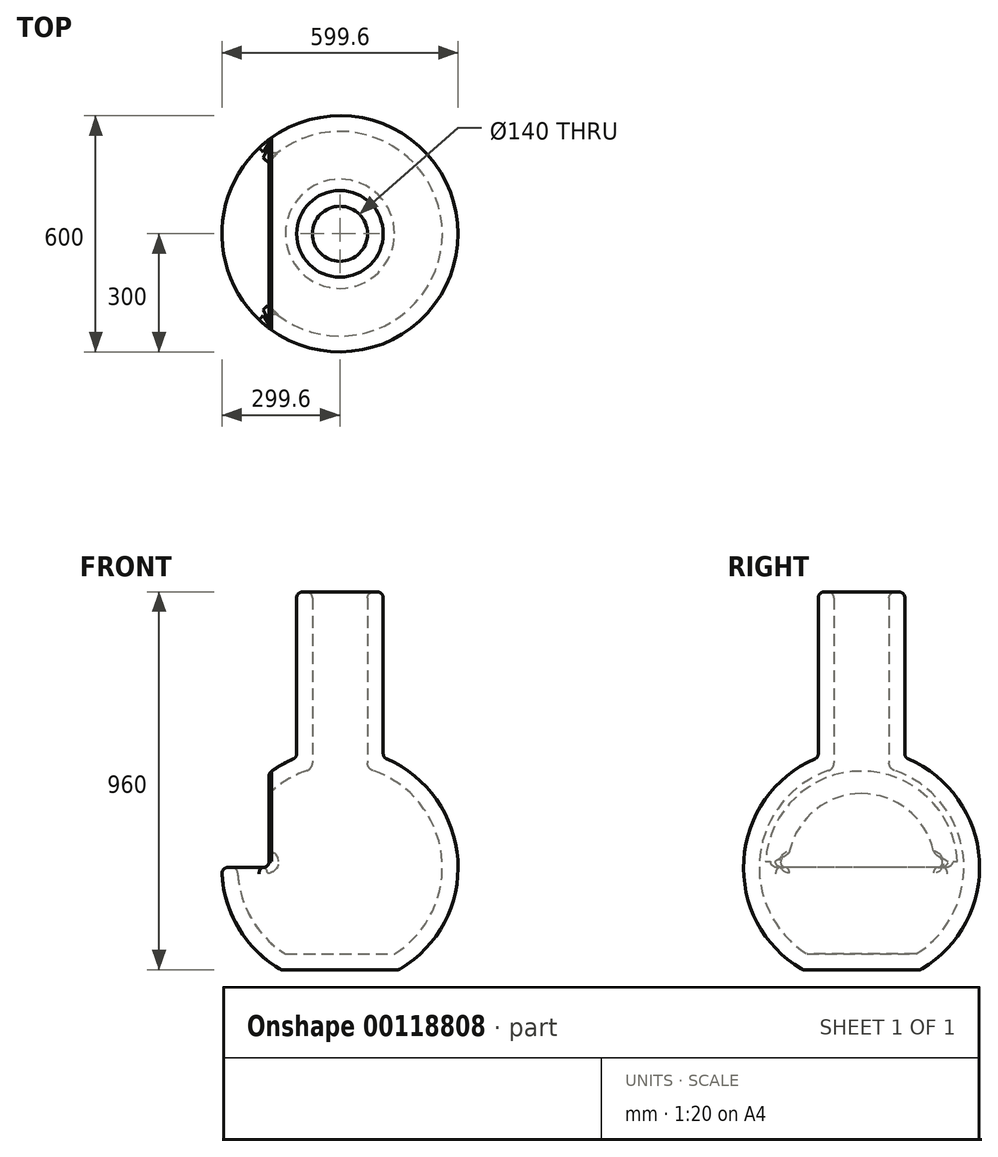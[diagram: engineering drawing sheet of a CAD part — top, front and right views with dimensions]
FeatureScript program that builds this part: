
annotation { "Feature Type Name" : "Feature", "Feature Type Description" : "" }
export const myFeature = defineFeature(function(context is Context, id is Id, definition is map)
    precondition{}
    {
        {
            var Q0;
            Q0=qCreatedBy(makeId("Front.planeOp"),FACE);
            var sketch = newSketch(context, id + "F0", { "sketchPlane" : qUnion([Q0])});
            skArc(sketch, "E0", {"start": v(0, 300) * mm, "mid": v(-254.47, 158.89) * mm, "end": v(-269.55, -131.7) * mm});
            skLineSegment(sketch, "E1", {"start": v(0, -260) * mm, "end": v(0, 700) * mm});
            skLineSegment(sketch, "E2", {"start": v(0, 700) * mm, "end": v(-110, 700) * mm});
            skLineSegment(sketch, "E3", {"start": v(-110, 700) * mm, "end": v(-110, 279.1) * mm});
            skLineSegment(sketch, "E4", {"start": v(0, 0) * mm, "end": v(-300, 0) * mm});
            skLineSegment(sketch, "E5", {"start": v(0, -260) * mm, "end": v(-149.67, -260) * mm});
            skLineSegment(sketch, "E6", {"start": v(0, -131.7) * mm, "end": v(-269.55, -131.7) * mm});
            skLineSegment(sketch, "E7", {"start": v(-180, 240) * mm, "end": v(-180, 0) * mm});
            skLineSegment(sketch, "E8", {"start": v(-180, 240) * mm, "end": v(0, 240) * mm});
            skArc(sketch, "E9", {"start": v(-269.55, -131.7) * mm, "mid": v(-219.2, -204.82) * mm, "end": v(-149.67, -260) * mm});
            skLineSegment(sketch, "E10", {"start": v(-269.55, -131.7) * mm, "end": v(-269.55, -131.7) * mm});
            skLineSegment(sketch, "E11", {"start": v(0, 131.7) * mm, "end": v(-269.55, 131.7) * mm});
            skSolve(sketch);
        }
        {
            var Q0;
            {var subQ0=sQuery(id+"F0.wireOp",EDGE,"E4");var subQ1=sQuery(id+"F0.wireOp",EDGE,"E0");var subQ2=makeQuery(id+"F0.imprint","INTERSECT",VERTEX,{"derivedFrom":[subQ1,subQ0]});Q0=makeQuery(id+"F0.imprint","IMPRINT",FACE,{"disambiguationData":[TD([[makeQuery(id+"F0.imprint","IMPRINT",EDGE,{"disambiguationData":[TD([[subQ2,1.0]])],"derivedFrom":subQ0}),-1.0]])]});}
            var Q1;
            {var subQ6=sQuery(id+"F0.wireOp",EDGE,"E6");Q1=makeQuery(id+"F0.imprint","IMPRINT",FACE,{"disambiguationData":[TD([[makeQuery(id+"F0.imprint","IMPRINT",EDGE,{"derivedFrom":subQ6}),-1.0]])]});}
            var Q2;
            {var subQ0=sQuery(id+"F0.wireOp",EDGE,"E5");Q2=makeQuery(id+"F0.imprint","IMPRINT",FACE,{"disambiguationData":[TD([[makeQuery(id+"F0.imprint","IMPRINT",EDGE,{"derivedFrom":subQ0}),-1.0]])]});}
            var Q3;
            {var subQ0=sQuery(id+"F0.wireOp",EDGE,"6abcfe9a-e38b-4595-b48a-67f45f4695cf0.MirrorCS");Q3=makeQuery(id+"F0.imprint","IMPRINT",FACE,{"disambiguationData":[TD([[makeQuery(id+"F0.imprint","IMPRINT",EDGE,{"derivedFrom":subQ0}),1.0]])]});}
            var Q4;
            {var subQ4=sQuery(id+"F0.wireOp",EDGE,"6abcfe9a-e38b-4595-b48a-67f45f4695cf0.MirrorCS");Q4=makeQuery(id+"F0.imprint","IMPRINT",FACE,{"disambiguationData":[TD([[makeQuery(id+"F0.imprint","IMPRINT",EDGE,{"derivedFrom":subQ4}),-1.0]])]});}
            var Q5;
            {var subQ4=sQuery(id+"F0.wireOp",EDGE,"E2");Q5=makeQuery(id+"F0.imprint","IMPRINT",FACE,{"disambiguationData":[TD([[makeQuery(id+"F0.imprint","IMPRINT",EDGE,{"derivedFrom":subQ4}),1.0]])]});}
            var Q6;
            {var subQ0=sQuery(id+"F0.wireOp",EDGE,"E8");Q6=makeQuery(id+"F0.imprint","IMPRINT",FACE,{"disambiguationData":[TD([[makeQuery(id+"F0.imprint","IMPRINT",EDGE,{"derivedFrom":subQ0}),-1.0]])]});}
            var Q7;
            {var subQ1=sQuery(id+"F0.wireOp",EDGE,"E0");var subQ3=sQuery(id+"F0.wireOp",EDGE,"E11");var subQ4=makeQuery(id+"F0.imprint","INTERSECT",VERTEX,{"derivedFrom":[subQ1,subQ3]});Q7=makeQuery(id+"F0.imprint","IMPRINT",FACE,{"disambiguationData":[TD([[makeQuery(id+"F0.imprint","IMPRINT",EDGE,{"disambiguationData":[TD([[subQ4,1.0]])],"derivedFrom":subQ3}),-1.0]])]});}
            var Q8;
            {var subQ0=sQuery(id+"F0.wireOp",EDGE,"E4");var subQ1=sQuery(id+"F0.wireOp",EDGE,"E1");var subQ2=makeQuery(id+"F0.imprint","INTERSECT",VERTEX,{"derivedFrom":[subQ1,subQ0]});Q8=makeQuery(id+"F0.imprint","IMPRINT",FACE,{"disambiguationData":[TD([[makeQuery(id+"F0.imprint","IMPRINT",EDGE,{"disambiguationData":[TD([[subQ2,-1.0]])],"derivedFrom":subQ1}),1.0]])]});}
            var Q9;
            {var subQ4=sQuery(id+"F0.wireOp",EDGE,"E8");Q9=makeQuery(id+"F0.imprint","IMPRINT",FACE,{"disambiguationData":[TD([[makeQuery(id+"F0.imprint","IMPRINT",EDGE,{"derivedFrom":subQ4}),1.0]])]});}
            var Q10;
            Q10=sQuery(id+"F0.wireOp",EDGE,"E1");
            revolve(context, id + "F1", {"entities" : qUnion([Q0, Q1, Q2, Q3, Q4, Q5, Q6, Q7, Q8, Q9]), "axis" : qUnion([Q10]), "revolveType" : RevolveType.FULL});
        }
        {
            var Q0;
            Q0=makeQuery(id+"F1.opRevolve","CAP_FACE",FACE,{"disambiguationData":[OSD([sQuery(id+"F0.wireOp",EDGE,"E0"),sQuery(id+"F0.wireOp",EDGE,"E1"),sQuery(id+"F0.wireOp",EDGE,"E2"),sQuery(id+"F0.wireOp",EDGE,"E3"),sQuery(id+"F0.wireOp",EDGE,"E5"),sQuery(id+"F0.wireOp",EDGE,"E9")])],"isStart":true});
            var Q1;
            Q1=makeQuery(id+"F1.opRevolve","SWEPT_FACE",FACE,{"disambiguationData":[OSD([sQuery(id+"F0.wireOp",EDGE,"E2")])]});
            shell(context, id + "F2", {"entities" : qUnion([Q0, Q1]), "thickness" : 40 * mm});
        }
        {
            var Q0;
            {var subQ0=sQuery(id+"F0.wireOp",EDGE,"E4");var subQ1=sQuery(id+"F0.wireOp",EDGE,"E0");var subQ2=makeQuery(id+"F0.imprint","INTERSECT",VERTEX,{"derivedFrom":[subQ1,subQ0]});Q0=makeQuery(id+"F0.imprint","IMPRINT",FACE,{"disambiguationData":[TD([[makeQuery(id+"F0.imprint","IMPRINT",EDGE,{"disambiguationData":[TD([[subQ2,1.0]])],"derivedFrom":subQ1}),1.0]])]});}
            var Q1;
            {var subQ1=sQuery(id+"F0.wireOp",EDGE,"E0");var subQ3=sQuery(id+"F0.wireOp",EDGE,"E11");var subQ4=makeQuery(id+"F0.imprint","INTERSECT",VERTEX,{"derivedFrom":[subQ1,subQ3]});Q1=makeQuery(id+"F0.imprint","IMPRINT",FACE,{"disambiguationData":[TD([[makeQuery(id+"F0.imprint","IMPRINT",EDGE,{"disambiguationData":[TD([[subQ4,1.0]])],"derivedFrom":subQ3}),-1.0]])]});}
            extrude(context, id + "F3", {"entities" : qUnion([Q0, Q1]), "operationType" : NewBodyOperationType.REMOVE, "endBound" : BoundingType.THROUGH_ALL, "oppositeDirection" : true, "depth" : 25 * mm, "hasSecondDirection" : true, "secondDirectionOppositeDirection" : false, "secondDirectionDepth" : 255.08 * mm});
        }
        {
            var Q0;
            Q0=makeQuery(id+"F3.boolean.opBoolean","COPY",FACE,{"derivedFrom":makeQuery(id+"F3.opExtrude","SWEPT_FACE",FACE,{"disambiguationData":[OSD([sQuery(id+"F0.wireOp",EDGE,"E4")])]})});
            var Q1;
            Q1=makeQuery(id+"F1.opRevolve","SWEPT_FACE",FACE,{"disambiguationData":[OSD([sQuery(id+"F0.wireOp",EDGE,"E0"),sQuery(id+"F0.wireOp",EDGE,"E9")])]});
            fillet(context, id + "F4", {"entities" : qUnion([Q0, Q1]), "radius" : 15 * mm, "tangentPropagation" : true, "allowEdgeOverflow" : false});
        }
        {
            var Q0;
            Q0=makeQuery(id+"F1.opRevolve","SWEPT_FACE",FACE,{"disambiguationData":[OSD([sQuery(id+"F0.wireOp",EDGE,"E2")])]});
            fillet(context, id + "F5", {"entities" : qUnion([Q0]), "radius" : 15 * mm, "tangentPropagation" : true, "allowEdgeOverflow" : false});
        }
        {
            var Q0;
            Q0=makeQuery(id+"F2.opShell","OFFSET_EDGE",EDGE,{"disambiguationData":[OSD([sQuery(id+"F0.wireOp",EDGE,"E0"),sQuery(id+"F0.wireOp",EDGE,"E3")])]});
            fillet(context, id + "F6", {"entities" : qUnion([Q0]), "radius" : 20 * mm, "tangentPropagation" : true, "allowEdgeOverflow" : false});
        }
    });
